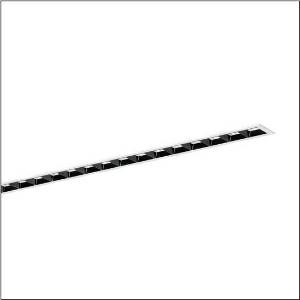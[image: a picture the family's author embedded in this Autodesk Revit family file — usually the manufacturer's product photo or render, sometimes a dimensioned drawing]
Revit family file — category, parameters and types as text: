
# Revit family: silica_21_51mx14da44wb
name_source: partatom
category: Lighting Fixtures
units: mm (PartAtom-declared; Revit-internal decimal feet)

## family parameters
Cut with Voids When Loaded = No
Host = Face
Light Source = No
Part Type = Normal
Room Calculation Point = No
Round Connector Dimension = Use Diameter
Shared = No

## types (1)
- --- (1 x LED, 4320 lm, 30 W, 4000K)
    Apparent Load = 30 VA
    CIE Flux Codes = 74 94 99 100 100
    Color Rendering = 80
    Color Temperature = 4000K
    Default Elevation = 1800 mm
    Description = Silica 21, office luminaire, primary light control with darklight reflector, of PMMA, black, light emission: direct distribution, primary light characteristic: asymmetric, installation type: recessed, LED, rated luminous flux: 4.320lm, luminous efficacy: 144lm/W, light colour: 840, colour temperature: 4000K, control gear: DALI 2, with terminal, 3+2-pole, max. 2.5mm², mains connection: 220..240V, AC, 50/60Hz, rated input power: 30W, luminaire housing, of aluminium, traffic white (RAL 9016), length: 1.228mm, width: 79mm, height: 53mm, protection rating (complete): IP20, insulation class (complete): insulation class I (protective earthing), certification: CE, ENEC, VDE, permissible operating ambient temperature: 0..+35°C, standard: EN 50419, packaging unit: 1 piece
    Height = 0 mm  [stored 0 ft]
    Lamp = 1 x LED
    Lamp Light Flux = 4320 lm
    Lamp Power = 30 W
    Lamp count = 1
    Length = 1227 mm
    Luminous efficacy = 144 lm/W
    Manufacturer = Siteco
    ModVariant = No
    Model = 51MX14DA44WB
    Mounting Place = Ceiling
    Mounting Type = Recessed
    Number of Poles = 1
    OnlyDefault = Yes
    Power Factor = 1
    Product Name = Silica 21
    Product group = office luminaire | ceiling recessed
    ProductGroupID = 400
    Protection Class = Protection class I
    Protection Degree = IP 20
    RLX_Detail_Level = 1
    RLX_Emergency_Light_Flux = 0 lm
    RLX_Emergency_Type = 0
    RLX_Emergency_Type_DB = No
    RlxData = <blob elided: 40513 chars, md5=e907aac4>
    Socket = socket
    Standby Power = 0 W
    System Light Flux = 4320 lm
    System Power = 30 W
    Type Comments = factory setting: luminous flux: 100 % | dim-lin: 254 | 418 mA
    Type Image = l_1335880.jpg
    URL = http://relux.com
    VarID = @adj_122697
    Voltage = 0 V
    Weight = 0.00 kg
    Width = 79 mm

note: [stored X ft] marks values corroborated as IEEE doubles in the binary element streams (Revit-internal decimal feet)

## geometry (parser evidence)
native form markers: Blend x4, Sweep x10
no freeform markers — native parametric forms only
